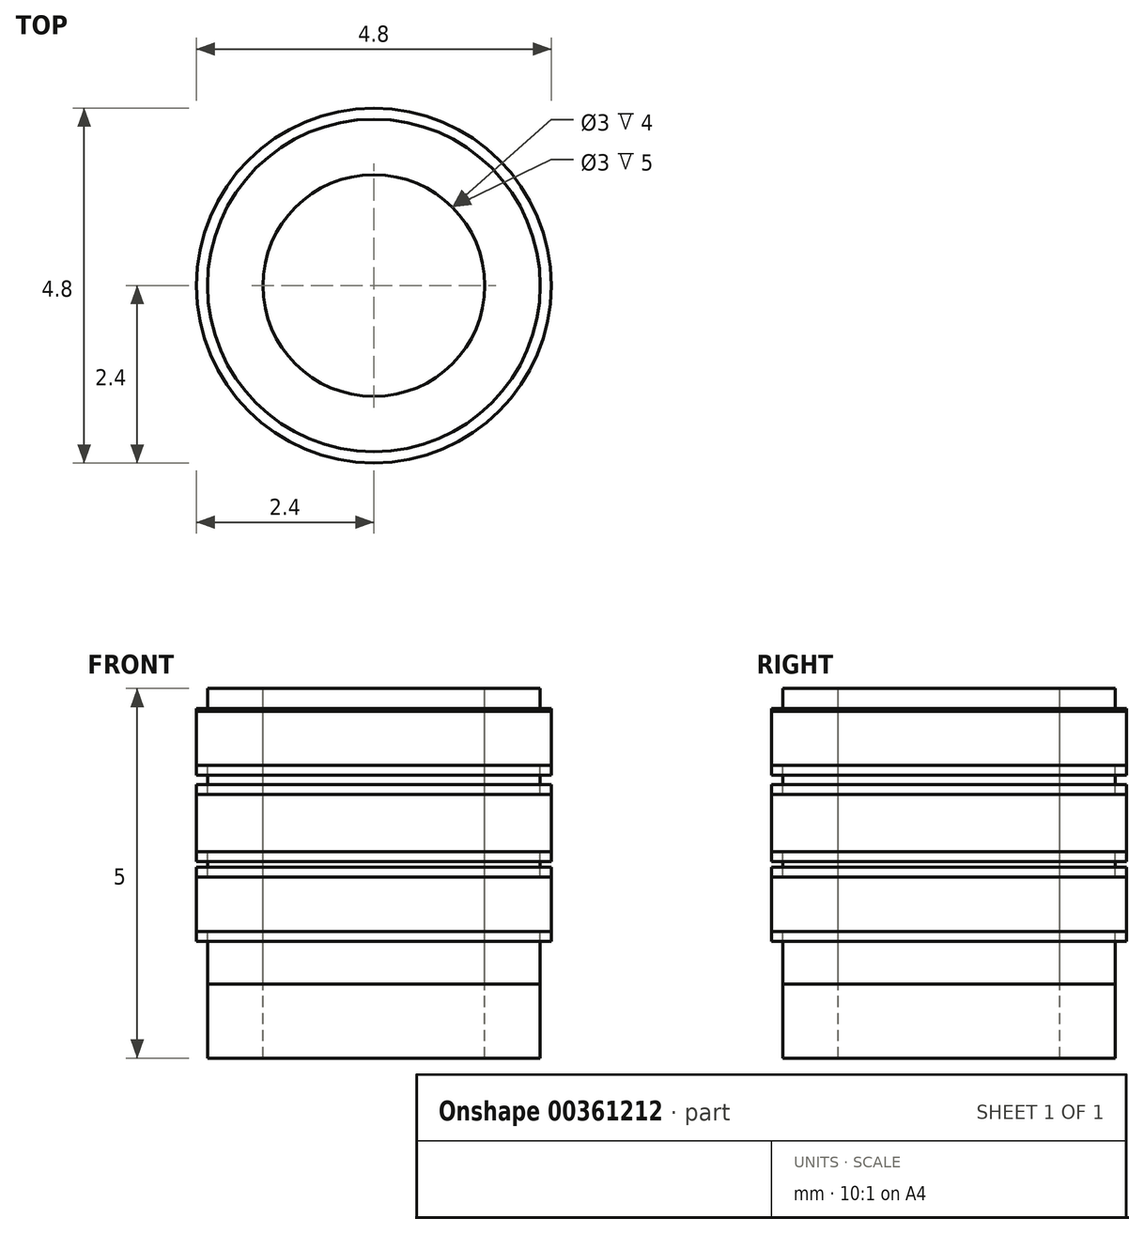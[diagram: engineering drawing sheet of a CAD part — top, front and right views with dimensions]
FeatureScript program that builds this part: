
annotation { "Feature Type Name" : "Feature", "Feature Type Description" : "" }
export const myFeature = defineFeature(function(context is Context, id is Id, definition is map)
    precondition{}
    {
        {
            var Q0;
            Q0=qCreatedBy(makeId("Front.planeOp"),FACE);
            var sketch = newSketch(context, id + "F0", { "sketchPlane" : qUnion([Q0])});
            skLineSegment(sketch, "E0", {"start": v(1.5, 0) * mm, "end": v(2.25, 0) * mm});
            skLineSegment(sketch, "E1", {"start": v(2.25, 0) * mm, "end": v(2.25, -5) * mm});
            skLineSegment(sketch, "E2", {"start": v(2.25, -5) * mm, "end": v(1.5, -5) * mm});
            skLineSegment(sketch, "E3", {"start": v(1.5, 0) * mm, "end": v(1.5, -5) * mm});
            skPoint(sketch, "E4.end.orphan", {"position": v(0, 0) * mm});
            skPoint(sketch, "E5.orphan", {"position": v(0, -5) * mm});
            skLineSegment(sketch, "E6.bottom", {"start": v(2.25, -0.31) * mm, "end": v(2.4, -0.31) * mm});
            skLineSegment(sketch, "E6.top", {"start": v(2.25, -1.17) * mm, "end": v(2.4, -1.17) * mm});
            skLineSegment(sketch, "E6.left", {"start": v(2.25, -0.31) * mm, "end": v(2.25, -1.17) * mm});
            skLineSegment(sketch, "E6.right", {"start": v(2.4, -0.31) * mm, "end": v(2.4, -1.17) * mm});
            skLineSegment(sketch, "E7.bottom", {"start": v(2.25, -1.43) * mm, "end": v(2.4, -1.43) * mm});
            skLineSegment(sketch, "E7.top", {"start": v(2.25, -2.34) * mm, "end": v(2.4, -2.34) * mm});
            skLineSegment(sketch, "E7.left", {"start": v(2.25, -1.43) * mm, "end": v(2.25, -2.34) * mm});
            skLineSegment(sketch, "E7.right", {"start": v(2.4, -1.43) * mm, "end": v(2.4, -2.34) * mm});
            skLineSegment(sketch, "E8.bottom", {"start": v(2.25, -2.55) * mm, "end": v(2.4, -2.55) * mm});
            skLineSegment(sketch, "E8.top", {"start": v(2.25, -3.42) * mm, "end": v(2.4, -3.42) * mm});
            skLineSegment(sketch, "E8.left", {"start": v(2.25, -2.55) * mm, "end": v(2.25, -3.42) * mm});
            skLineSegment(sketch, "E8.right", {"start": v(2.4, -2.55) * mm, "end": v(2.4, -3.42) * mm});
            skLineSegment(sketch, "E9", {"start": v(0, 0) * mm, "end": v(0, -1.04) * mm, "construction": true});
            skSolve(sketch);
        }
        {
            var Q0;
            Q0 = qSketchRegion(id + "F0", true);
            var Q1;
            Q1=sQuery(id+"F0.wireOp",EDGE,"E9");
            revolve(context, id + "F1", {"surfaceOperationType" : NewSurfaceOperationType.NEW, "entities" : qUnion([Q0]), "axis" : qUnion([Q1]), "revolveType" : RevolveType.FULL});
        }
        {
            var Q0;
            Q0=qCreatedBy(makeId("Front.planeOp"),FACE);
            var sketch = newSketch(context, id + "F2", { "sketchPlane" : qUnion([Q0])});
            skLineSegment(sketch, "E10", {"start": v(1.5, 0) * mm, "end": v(2.25, 0) * mm});
            skLineSegment(sketch, "E11", {"start": v(2.25, 0) * mm, "end": v(2.25, -4) * mm});
            skLineSegment(sketch, "E12", {"start": v(2.25, -4) * mm, "end": v(1.5, -4) * mm});
            skLineSegment(sketch, "E13", {"start": v(1.5, 0) * mm, "end": v(1.5, -4) * mm});
            skPoint(sketch, "E14.end.orphan", {"position": v(0, 0) * mm});
            skPoint(sketch, "E15.orphan", {"position": v(-5.68, -4) * mm});
            skLineSegment(sketch, "E16.bottom", {"start": v(2.25, -0.27) * mm, "end": v(2.4, -0.27) * mm});
            skLineSegment(sketch, "E16.top", {"start": v(2.25, -1.04) * mm, "end": v(2.4, -1.04) * mm});
            skLineSegment(sketch, "E16.left", {"start": v(2.25, -0.27) * mm, "end": v(2.25, -1.04) * mm});
            skLineSegment(sketch, "E16.right", {"start": v(2.4, -0.27) * mm, "end": v(2.4, -1.04) * mm});
            skLineSegment(sketch, "E17.bottom", {"start": v(2.25, -1.3) * mm, "end": v(2.4, -1.3) * mm});
            skLineSegment(sketch, "E17.top", {"start": v(2.25, -2.21) * mm, "end": v(2.4, -2.21) * mm});
            skLineSegment(sketch, "E17.left", {"start": v(2.25, -1.3) * mm, "end": v(2.25, -2.21) * mm});
            skLineSegment(sketch, "E17.right", {"start": v(2.4, -1.3) * mm, "end": v(2.4, -2.21) * mm});
            skLineSegment(sketch, "E18.bottom", {"start": v(2.25, -2.42) * mm, "end": v(2.4, -2.42) * mm});
            skLineSegment(sketch, "E18.top", {"start": v(2.25, -3.29) * mm, "end": v(2.4, -3.29) * mm});
            skLineSegment(sketch, "E18.left", {"start": v(2.25, -2.42) * mm, "end": v(2.25, -3.29) * mm});
            skLineSegment(sketch, "E18.right", {"start": v(2.4, -2.42) * mm, "end": v(2.4, -3.29) * mm});
            skLineSegment(sketch, "E19", {"start": v(0, 0) * mm, "end": v(0, -4.66) * mm, "construction": true});
            skSolve(sketch);
        }
        {
            var Q0;
            Q0 = qSketchRegion(id + "F2", true);
            var Q1;
            Q1=sQuery(id+"F2.wireOp",EDGE,"E19");
            revolve(context, id + "F3", {"surfaceOperationType" : NewSurfaceOperationType.NEW, "entities" : qUnion([Q0]), "axis" : qUnion([Q1]), "revolveType" : RevolveType.FULL});
        }
    });
